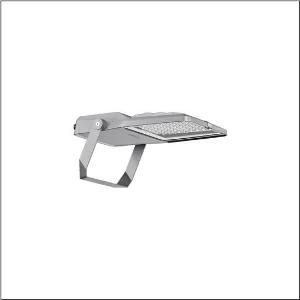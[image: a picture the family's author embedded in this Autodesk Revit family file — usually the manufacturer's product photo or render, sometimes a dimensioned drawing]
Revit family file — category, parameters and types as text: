
# Revit family: floodlight_fl_21_iq_mini___pl43_5xa7772d2a1a_725a
name_source: partatom
category: Lighting Fixtures
units: mm (PartAtom-declared; Revit-internal decimal feet)

## family parameters
Cut with Voids When Loaded = No
Host = Face
Light Source = No
Part Type = Normal
Room Calculation Point = No
Round Connector Dimension = Use Diameter
Shared = No

## types (1)
- --- (1 x LED, 18290 lm, 143 W, 3000K)
    Apparent Load = 143 VA
    CIE Flux Codes = 27 78 99 100 100
    Color Rendering = 70
    Color Temperature = 3000K
    Default Elevation = 1800 mm
    Description = Floodlight FL 21 iQ mini, floodlight, primary light control with lens, of PMMA, primary optical cover: protective disc, of toughened safety glass, transparent, light distribution: PL43, light emission: direct distribution, installation type: surface-mounted, lamps: LED, High Power LED, rated values: 18.290lm | 143W | 127,9lm/W (begin service life); end service life: 18.290lm | 151,6W; at 50% lumin. flux: 9.145lm | 60,6W | 150,9lm/W, colour temperature: 3000K, colour rendering: CRI > 70, light colour: 730, light setting 1 begin service life: 100% | 18.290lm | 143W | 127,9lm/W | 3.000K, light setting 1 end service life: 151,6W, further light settings possible, control: Street-Remote, Auto-Match, Temp-Guard, Night-Set, Smart-Wire, Desk-Remote (wireless, voltage-free reading and setting of iQ features in the workshop via application-optimized NFC function/RFID function), optimised constant luminous flux control (CLO 2.0), pre-setting: linear dimming characteristic, with terminal, 6-pole, mains connection: 220..240V, AC, 50/60Hz, luminaire housing, of diecast aluminium, powder-coated, SITECO metallic grey (DB 702S), corrosivity category C5 mid according to DIN EN ISO 12944suitable for swimming poolschlorine-resistant, sealing non-destructively replaceable, mounting bracket, of steel, galvanised, powder-coated, SITECO metallic grey (DB 702S), protection rating (complete): IP66, insulation class (complete): insulation class II (safety insulation), certification: CE, ENEC, VDE, protection symbol: D, impact resistance: IK08, permissible operating ambient temperature: -40..+40°C, permissible operating ambient temperature for outdoor applications: -40..+50°C, standard: DIN EN 12944, LABS conformity tested according to VDMA 24364:2018-05, packaging unit: 1 piece

Light Distribution: PL43
    Height = 70 mm
    Lamp = 1 x LED
    Lamp Light Flux = 18290 lm
    Lamp Power = 143 W
    Lamp count = 1
    Length = 485 mm
    Luminous efficacy = 128 lm/W
    Manufacturer = Siteco
    ModVariant = No
    Model = 5XA7772D2A1A
    Mounting Place = Pole
    Mounting Type = Pole annexe
    Number of Poles = 1
    OnlyDefault = Yes
    Power Factor = 1
    Product Name = Floodlight FL 21 iQ mini | PL43
    Product group = floodlight | pylon annexe
    ProductGroupID = 6201
    Protection Class = Protection class II
    Protection Degree = IP 66
    RLX_Detail_Level = 1
    RLX_Emergency_Light_Flux = 0 lm
    RLX_Emergency_Type = 0
    RLX_Emergency_Type_DB = No
    RlxData = <blob elided: 96793 chars, md5=06188bdb>
    Socket = socket
    Standby Power = 0 W
    System Light Flux = 18290 lm
    System Power = 143 W
    Type Comments = factory setting: luminous flux: 100 % | dim-lin: 254 | 730 mA
    Type Image = l_1006845.jpg
    URL = http://relux.com
    VarID = @adj_163067
    Voltage = 0 V
    Weight = 0.00 kg
    Width = 337 mm

## geometry (parser evidence)
native form markers: Blend x4, Sweep x15
no freeform markers — native parametric forms only
